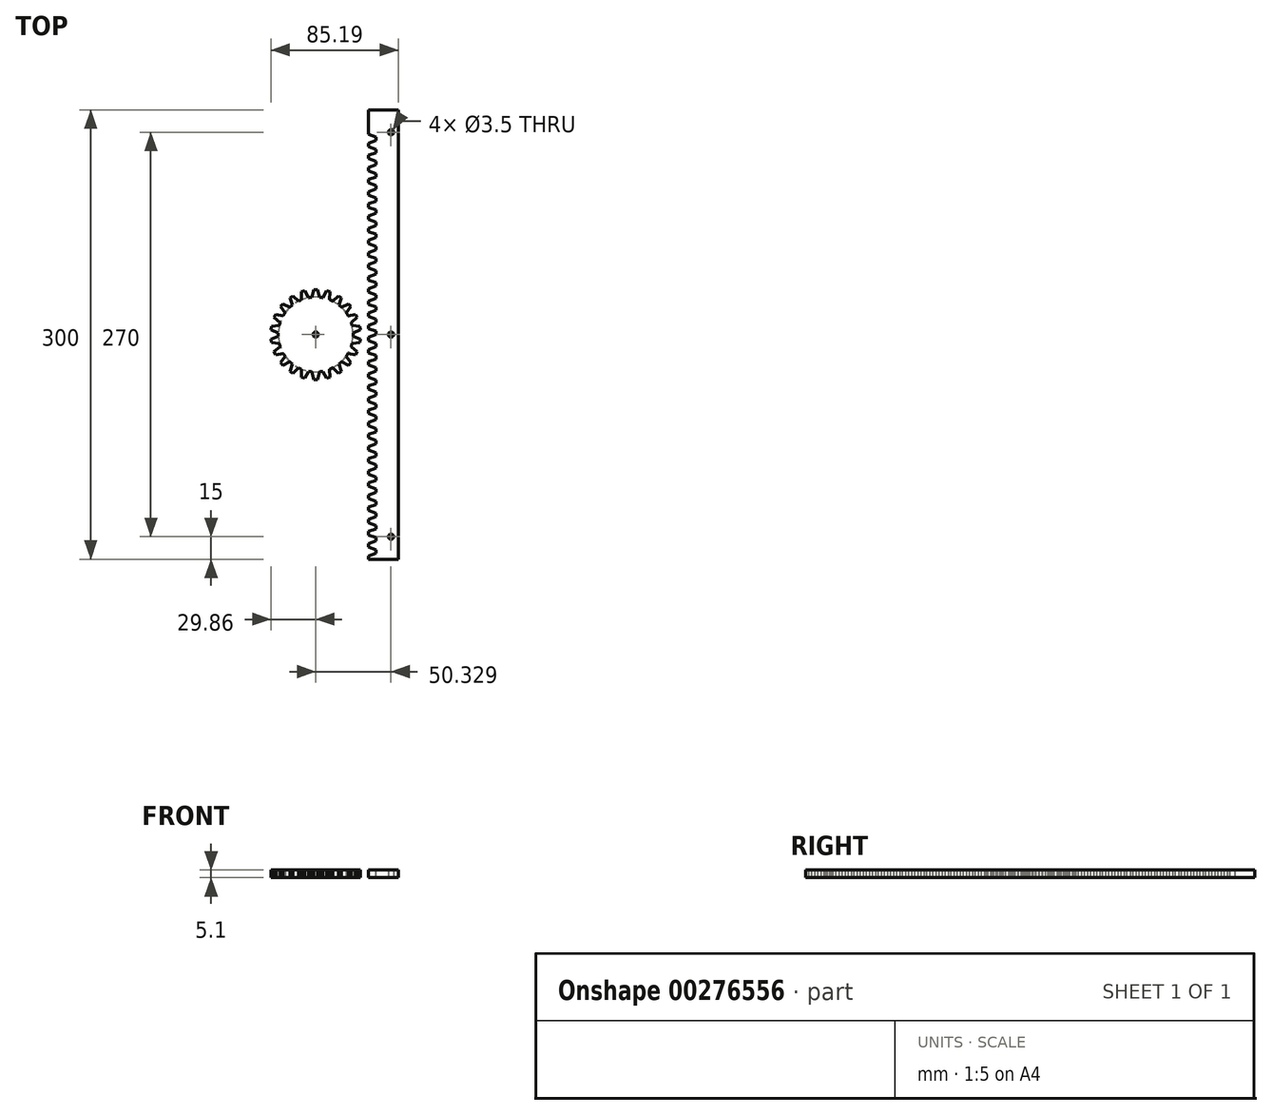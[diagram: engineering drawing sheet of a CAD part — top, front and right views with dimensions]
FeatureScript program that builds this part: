
annotation { "Feature Type Name" : "Feature", "Feature Type Description" : "" }
export const myFeature = defineFeature(function(context is Context, id is Id, definition is map)
    precondition{}
    {
        {
            var Q0;
            Q0=qCreatedBy(makeId("Top.planeOp"),FACE);
            var sketch = newSketch(context, id + "F0", { "sketchPlane" : qUnion([Q0])});
            skCircle(sketch, "E0", {"center": v(0, 0) * mm, "radius": 25 * mm});
            skSolve(sketch);
        }
        {
            var Q0;
            Q0 = qSketchRegion(id + "F0", true);
            extrude(context, id + "F1", {"entities" : qUnion([Q0]), "depth" : .1 * mm});
        }
        {
            var Q0;
            Q0=makeQuery(id+"F1.opExtrude","CAP_FACE",FACE,{"disambiguationData":[OSD([sQuery(id+"F0.wireOp",EDGE,"E0")])],"isStart":false});
            var sketch = newSketch(context, id + "F2", { "sketchPlane" : qUnion([Q0])});
            skLineSegment(sketch, "E1", {"start": v(0, 0) * mm, "end": v(3.22, 32.66) * mm, "construction": true});
            skLineSegment(sketch, "E2", {"start": v(0, 0) * mm, "end": v(-3.22, 32.7) * mm, "construction": true});
            skLineSegment(sketch, "E3", {"start": v(-2.45, 24.88) * mm, "end": v(-1.14, 30) * mm});
            skLineSegment(sketch, "E4", {"start": v(-1.14, 30) * mm, "end": v(1.14, 30) * mm});
            skLineSegment(sketch, "E5", {"start": v(1.14, 30) * mm, "end": v(2.45, 24.88) * mm});
            skLineSegment(sketch, "E6.1.0", {"start": v(-9.36, 23.18) * mm, "end": v(-9.54, 28.46) * mm});
            skLineSegment(sketch, "E6.1.1", {"start": v(-7.36, 29.1) * mm, "end": v(-4.66, 24.56) * mm});
            skLineSegment(sketch, "E6.1.2", {"start": v(-9.54, 28.46) * mm, "end": v(-7.36, 29.1) * mm});
            skLineSegment(sketch, "E6.2.0", {"start": v(-15.51, 19.6) * mm, "end": v(-17.18, 24.62) * mm});
            skLineSegment(sketch, "E6.2.1", {"start": v(-15.26, 25.85) * mm, "end": v(-11.39, 22.25) * mm});
            skLineSegment(sketch, "E6.2.2", {"start": v(-17.18, 24.62) * mm, "end": v(-15.26, 25.85) * mm});
            skLineSegment(sketch, "E6.3.0", {"start": v(-20.4, 14.44) * mm, "end": v(-23.42, 18.79) * mm});
            skLineSegment(sketch, "E6.3.1", {"start": v(-21.93, 20.5) * mm, "end": v(-17.2, 18.14) * mm});
            skLineSegment(sketch, "E6.3.2", {"start": v(-23.42, 18.79) * mm, "end": v(-21.93, 20.5) * mm});
            skLineSegment(sketch, "E6.4.0", {"start": v(-23.65, 8.1) * mm, "end": v(-27.76, 11.43) * mm});
            skLineSegment(sketch, "E6.4.1", {"start": v(-26.82, 13.5) * mm, "end": v(-21.61, 12.56) * mm});
            skLineSegment(sketch, "E6.4.2", {"start": v(-27.76, 11.43) * mm, "end": v(-26.82, 13.5) * mm});
            skLineSegment(sketch, "E6.5.0", {"start": v(-24.98, 1.12) * mm, "end": v(-29.86, 3.14) * mm});
            skLineSegment(sketch, "E6.5.1", {"start": v(-29.53, 5.4) * mm, "end": v(-24.28, 5.97) * mm});
            skLineSegment(sketch, "E6.5.2", {"start": v(-29.86, 3.14) * mm, "end": v(-29.53, 5.4) * mm});
            skLineSegment(sketch, "E6.6.0", {"start": v(-24.28, -5.97) * mm, "end": v(-29.53, -5.4) * mm});
            skLineSegment(sketch, "E6.6.1", {"start": v(-29.86, -3.14) * mm, "end": v(-24.98, -1.12) * mm});
            skLineSegment(sketch, "E6.6.2", {"start": v(-29.53, -5.4) * mm, "end": v(-29.86, -3.14) * mm});
            skLineSegment(sketch, "E6.7.0", {"start": v(-21.61, -12.56) * mm, "end": v(-26.82, -13.5) * mm});
            skLineSegment(sketch, "E6.7.1", {"start": v(-27.76, -11.43) * mm, "end": v(-23.65, -8.1) * mm});
            skLineSegment(sketch, "E6.7.2", {"start": v(-26.82, -13.5) * mm, "end": v(-27.76, -11.43) * mm});
            skLineSegment(sketch, "E6.8.0", {"start": v(-17.2, -18.14) * mm, "end": v(-21.93, -20.5) * mm});
            skLineSegment(sketch, "E6.8.1", {"start": v(-23.42, -18.79) * mm, "end": v(-20.4, -14.44) * mm});
            skLineSegment(sketch, "E6.8.2", {"start": v(-21.93, -20.5) * mm, "end": v(-23.42, -18.79) * mm});
            skLineSegment(sketch, "E6.9.0", {"start": v(-11.39, -22.25) * mm, "end": v(-15.26, -25.85) * mm});
            skLineSegment(sketch, "E6.9.1", {"start": v(-17.18, -24.62) * mm, "end": v(-15.51, -19.6) * mm});
            skLineSegment(sketch, "E6.9.2", {"start": v(-15.26, -25.85) * mm, "end": v(-17.18, -24.62) * mm});
            skLineSegment(sketch, "E6.10.0", {"start": v(-4.66, -24.56) * mm, "end": v(-7.36, -29.1) * mm});
            skLineSegment(sketch, "E6.10.1", {"start": v(-9.54, -28.46) * mm, "end": v(-9.36, -23.18) * mm});
            skLineSegment(sketch, "E6.10.2", {"start": v(-7.36, -29.1) * mm, "end": v(-9.54, -28.46) * mm});
            skLineSegment(sketch, "E6.11.0", {"start": v(2.45, -24.88) * mm, "end": v(1.14, -30) * mm});
            skLineSegment(sketch, "E6.11.1", {"start": v(-1.14, -30) * mm, "end": v(-2.45, -24.88) * mm});
            skLineSegment(sketch, "E6.11.2", {"start": v(1.14, -30) * mm, "end": v(-1.14, -30) * mm});
            skLineSegment(sketch, "E6.12.0", {"start": v(9.36, -23.18) * mm, "end": v(9.54, -28.46) * mm});
            skLineSegment(sketch, "E6.12.1", {"start": v(7.36, -29.1) * mm, "end": v(4.66, -24.56) * mm});
            skLineSegment(sketch, "E6.12.2", {"start": v(9.54, -28.46) * mm, "end": v(7.36, -29.1) * mm});
            skLineSegment(sketch, "E6.13.0", {"start": v(15.51, -19.6) * mm, "end": v(17.18, -24.62) * mm});
            skLineSegment(sketch, "E6.13.1", {"start": v(15.26, -25.85) * mm, "end": v(11.39, -22.25) * mm});
            skLineSegment(sketch, "E6.13.2", {"start": v(17.18, -24.62) * mm, "end": v(15.26, -25.85) * mm});
            skLineSegment(sketch, "E6.14.0", {"start": v(20.4, -14.44) * mm, "end": v(23.42, -18.79) * mm});
            skLineSegment(sketch, "E6.14.1", {"start": v(21.93, -20.5) * mm, "end": v(17.2, -18.14) * mm});
            skLineSegment(sketch, "E6.14.2", {"start": v(23.42, -18.79) * mm, "end": v(21.93, -20.5) * mm});
            skLineSegment(sketch, "E6.15.0", {"start": v(23.65, -8.1) * mm, "end": v(27.76, -11.43) * mm});
            skLineSegment(sketch, "E6.15.1", {"start": v(26.82, -13.5) * mm, "end": v(21.61, -12.56) * mm});
            skLineSegment(sketch, "E6.15.2", {"start": v(27.76, -11.43) * mm, "end": v(26.82, -13.5) * mm});
            skLineSegment(sketch, "E6.16.0", {"start": v(24.98, -1.12) * mm, "end": v(29.86, -3.14) * mm});
            skLineSegment(sketch, "E6.16.1", {"start": v(29.53, -5.4) * mm, "end": v(24.28, -5.97) * mm});
            skLineSegment(sketch, "E6.16.2", {"start": v(29.86, -3.14) * mm, "end": v(29.53, -5.4) * mm});
            skLineSegment(sketch, "E6.17.0", {"start": v(24.28, 5.97) * mm, "end": v(29.53, 5.4) * mm});
            skLineSegment(sketch, "E6.17.1", {"start": v(29.86, 3.14) * mm, "end": v(24.98, 1.12) * mm});
            skLineSegment(sketch, "E6.17.2", {"start": v(29.53, 5.4) * mm, "end": v(29.86, 3.14) * mm});
            skLineSegment(sketch, "E6.18.0", {"start": v(21.61, 12.56) * mm, "end": v(26.82, 13.5) * mm});
            skLineSegment(sketch, "E6.18.1", {"start": v(27.76, 11.43) * mm, "end": v(23.65, 8.1) * mm});
            skLineSegment(sketch, "E6.18.2", {"start": v(26.82, 13.5) * mm, "end": v(27.76, 11.43) * mm});
            skLineSegment(sketch, "E6.19.0", {"start": v(17.2, 18.14) * mm, "end": v(21.93, 20.5) * mm});
            skLineSegment(sketch, "E6.19.1", {"start": v(23.42, 18.79) * mm, "end": v(20.4, 14.44) * mm});
            skLineSegment(sketch, "E6.19.2", {"start": v(21.93, 20.5) * mm, "end": v(23.42, 18.79) * mm});
            skPoint(sketch, "E6.center", {"position": v(0, 0) * mm});
            skLineSegment(sketch, "E7.1.20.0", {"start": v(11.39, 22.25) * mm, "end": v(15.26, 25.85) * mm});
            skLineSegment(sketch, "E7.3.20.0", {"start": v(17.18, 24.62) * mm, "end": v(15.51, 19.6) * mm});
            skLineSegment(sketch, "E7.6.20.0", {"start": v(15.26, 25.85) * mm, "end": v(17.18, 24.62) * mm});
            skCircle(sketch, "E8", {"center": v(0, 0) * mm, "radius": 25.04 * mm});
            skLineSegment(sketch, "E9.1.21.0", {"start": v(4.66, 24.56) * mm, "end": v(7.36, 29.1) * mm});
            skLineSegment(sketch, "E9.3.21.0", {"start": v(9.54, 28.46) * mm, "end": v(9.36, 23.18) * mm});
            skLineSegment(sketch, "E9.6.21.0", {"start": v(7.36, 29.1) * mm, "end": v(9.54, 28.46) * mm});
            skSolve(sketch);
        }
        {
            var Q0;
            Q0 = qSketchRegion(id + "F2", true);
            extrude(context, id + "F3", {"entities" : qUnion([Q0]), "operationType" : NewBodyOperationType.ADD, "depth" : 5 * mm});
        }
        {
            var Q0;
            Q0=qCreatedBy(makeId("Top.planeOp"),FACE);
            var sketch = newSketch(context, id + "F4", { "sketchPlane" : qUnion([Q0])});
            skLineSegment(sketch, "E10.bottom", {"start": v(35.33, -150) * mm, "end": v(55.33, -150) * mm});
            skLineSegment(sketch, "E10.top", {"start": v(35.33, 150) * mm, "end": v(55.33, 150) * mm});
            skLineSegment(sketch, "E10.left", {"start": v(35.33, -150) * mm, "end": v(35.33, 150) * mm});
            skLineSegment(sketch, "E10.right", {"start": v(55.33, -150) * mm, "end": v(55.33, 150) * mm});
            skPoint(sketch, "E10.middle", {"position": v(45.33, 0) * mm});
            skSolve(sketch);
        }
        {
            var Q0;
            Q0 = qSketchRegion(id + "F4", true);
            extrude(context, id + "F5", {"entities" : qUnion([Q0]), "depth" : 5 * mm});
        }
        {
            var Q0;
            Q0=makeQuery(id+"F5.opExtrude","CAP_FACE",FACE,{"disambiguationData":[OSD([sQuery(id+"F4.wireOp",EDGE,"E10.bottom"),sQuery(id+"F4.wireOp",EDGE,"E10.top"),sQuery(id+"F4.wireOp",EDGE,"E10.left"),sQuery(id+"F4.wireOp",EDGE,"E10.right")])],"isStart":false});
            var sketch = newSketch(context, id + "F6", { "sketchPlane" : qUnion([Q0])});
            skLineSegment(sketch, "E11", {"start": v(35.33, -147.77) * mm, "end": v(40.33, -145.95) * mm});
            skLineSegment(sketch, "E12", {"start": v(40.33, -145.95) * mm, "end": v(40.33, -143.72) * mm});
            skLineSegment(sketch, "E13", {"start": v(40.33, -143.72) * mm, "end": v(35.33, -141.9) * mm});
            skLineSegment(sketch, "E14", {"start": v(35.33, -147.77) * mm, "end": v(35.33, -150) * mm});
            skLineSegment(sketch, "E15.1.0.0", {"start": v(40.33, -135.62) * mm, "end": v(35.33, -133.8) * mm});
            skLineSegment(sketch, "E15.1.0.1", {"start": v(35.33, -139.67) * mm, "end": v(40.33, -137.85) * mm});
            skLineSegment(sketch, "E15.1.0.2", {"start": v(35.33, -139.67) * mm, "end": v(35.33, -141.9) * mm});
            skLineSegment(sketch, "E15.1.0.3", {"start": v(40.33, -137.85) * mm, "end": v(40.33, -135.62) * mm});
            skLineSegment(sketch, "E15.2.0.0", {"start": v(40.33, -127.51) * mm, "end": v(35.33, -125.7) * mm});
            skLineSegment(sketch, "E15.2.0.1", {"start": v(35.33, -131.56) * mm, "end": v(40.33, -129.75) * mm});
            skLineSegment(sketch, "E15.2.0.2", {"start": v(35.33, -131.56) * mm, "end": v(35.33, -133.8) * mm});
            skLineSegment(sketch, "E15.2.0.3", {"start": v(40.33, -129.75) * mm, "end": v(40.33, -127.51) * mm});
            skLineSegment(sketch, "E15.3.0.0", {"start": v(40.33, -119.41) * mm, "end": v(35.33, -117.6) * mm});
            skLineSegment(sketch, "E15.3.0.1", {"start": v(35.33, -123.46) * mm, "end": v(40.33, -121.64) * mm});
            skLineSegment(sketch, "E15.3.0.2", {"start": v(35.33, -123.46) * mm, "end": v(35.33, -125.7) * mm});
            skLineSegment(sketch, "E15.3.0.3", {"start": v(40.33, -121.64) * mm, "end": v(40.33, -119.41) * mm});
            skLineSegment(sketch, "E15.4.0.0", {"start": v(40.33, -111.31) * mm, "end": v(35.33, -109.5) * mm});
            skLineSegment(sketch, "E15.4.0.1", {"start": v(35.33, -115.36) * mm, "end": v(40.33, -113.54) * mm});
            skLineSegment(sketch, "E15.4.0.2", {"start": v(35.33, -115.36) * mm, "end": v(35.33, -117.6) * mm});
            skLineSegment(sketch, "E15.4.0.3", {"start": v(40.33, -113.54) * mm, "end": v(40.33, -111.31) * mm});
            skLineSegment(sketch, "E15.5.0.0", {"start": v(40.33, -103.2) * mm, "end": v(35.33, -101.39) * mm});
            skLineSegment(sketch, "E15.5.0.1", {"start": v(35.33, -107.26) * mm, "end": v(40.33, -105.44) * mm});
            skLineSegment(sketch, "E15.5.0.2", {"start": v(35.33, -107.26) * mm, "end": v(35.33, -109.5) * mm});
            skLineSegment(sketch, "E15.5.0.3", {"start": v(40.33, -105.44) * mm, "end": v(40.33, -103.2) * mm});
            skLineSegment(sketch, "E15.6.0.0", {"start": v(40.33, -95.1) * mm, "end": v(35.33, -93.29) * mm});
            skLineSegment(sketch, "E15.6.0.1", {"start": v(35.33, -99.16) * mm, "end": v(40.33, -97.34) * mm});
            skLineSegment(sketch, "E15.6.0.2", {"start": v(35.33, -99.16) * mm, "end": v(35.33, -101.39) * mm});
            skLineSegment(sketch, "E15.6.0.3", {"start": v(40.33, -97.34) * mm, "end": v(40.33, -95.1) * mm});
            skLineSegment(sketch, "E15.7.0.0", {"start": v(40.33, -87) * mm, "end": v(35.33, -85.18) * mm});
            skLineSegment(sketch, "E15.7.0.1", {"start": v(35.33, -91.05) * mm, "end": v(40.33, -89.24) * mm});
            skLineSegment(sketch, "E15.7.0.2", {"start": v(35.33, -91.05) * mm, "end": v(35.33, -93.29) * mm});
            skLineSegment(sketch, "E15.7.0.3", {"start": v(40.33, -89.24) * mm, "end": v(40.33, -87) * mm});
            skLineSegment(sketch, "E15.8.0.0", {"start": v(40.33, -78.9) * mm, "end": v(35.33, -77.08) * mm});
            skLineSegment(sketch, "E15.8.0.1", {"start": v(35.33, -82.95) * mm, "end": v(40.33, -81.13) * mm});
            skLineSegment(sketch, "E15.8.0.2", {"start": v(35.33, -82.95) * mm, "end": v(35.33, -85.18) * mm});
            skLineSegment(sketch, "E15.8.0.3", {"start": v(40.33, -81.13) * mm, "end": v(40.33, -78.9) * mm});
            skLineSegment(sketch, "E15.9.0.0", {"start": v(40.33, -70.8) * mm, "end": v(35.33, -68.98) * mm});
            skLineSegment(sketch, "E15.9.0.1", {"start": v(35.33, -74.85) * mm, "end": v(40.33, -73.03) * mm});
            skLineSegment(sketch, "E15.9.0.2", {"start": v(35.33, -74.85) * mm, "end": v(35.33, -77.08) * mm});
            skLineSegment(sketch, "E15.9.0.3", {"start": v(40.33, -73.03) * mm, "end": v(40.33, -70.8) * mm});
            skLineSegment(sketch, "E15.10.0.0", {"start": v(40.33, -62.7) * mm, "end": v(35.33, -60.88) * mm});
            skLineSegment(sketch, "E15.10.0.1", {"start": v(35.33, -66.75) * mm, "end": v(40.33, -64.93) * mm});
            skLineSegment(sketch, "E15.10.0.2", {"start": v(35.33, -66.75) * mm, "end": v(35.33, -68.98) * mm});
            skLineSegment(sketch, "E15.10.0.3", {"start": v(40.33, -64.93) * mm, "end": v(40.33, -62.7) * mm});
            skLineSegment(sketch, "E15.11.0.0", {"start": v(40.33, -54.6) * mm, "end": v(35.33, -52.78) * mm});
            skLineSegment(sketch, "E15.11.0.1", {"start": v(35.33, -58.65) * mm, "end": v(40.33, -56.83) * mm});
            skLineSegment(sketch, "E15.11.0.2", {"start": v(35.33, -58.65) * mm, "end": v(35.33, -60.88) * mm});
            skLineSegment(sketch, "E15.11.0.3", {"start": v(40.33, -56.83) * mm, "end": v(40.33, -54.6) * mm});
            skLineSegment(sketch, "E15.12.0.0", {"start": v(40.33, -46.5) * mm, "end": v(35.33, -44.67) * mm});
            skLineSegment(sketch, "E15.12.0.1", {"start": v(35.33, -50.54) * mm, "end": v(40.33, -48.73) * mm});
            skLineSegment(sketch, "E15.12.0.2", {"start": v(35.33, -50.54) * mm, "end": v(35.33, -52.78) * mm});
            skLineSegment(sketch, "E15.12.0.3", {"start": v(40.33, -48.73) * mm, "end": v(40.33, -46.5) * mm});
            skLineSegment(sketch, "E15.13.0.0", {"start": v(40.33, -38.4) * mm, "end": v(35.33, -36.57) * mm});
            skLineSegment(sketch, "E15.13.0.1", {"start": v(35.33, -42.44) * mm, "end": v(40.33, -40.62) * mm});
            skLineSegment(sketch, "E15.13.0.2", {"start": v(35.33, -42.44) * mm, "end": v(35.33, -44.67) * mm});
            skLineSegment(sketch, "E15.13.0.3", {"start": v(40.33, -40.62) * mm, "end": v(40.33, -38.4) * mm});
            skLineSegment(sketch, "E15.14.0.0", {"start": v(40.33, -30.3) * mm, "end": v(35.33, -28.47) * mm});
            skLineSegment(sketch, "E15.14.0.1", {"start": v(35.33, -34.34) * mm, "end": v(40.33, -32.52) * mm});
            skLineSegment(sketch, "E15.14.0.2", {"start": v(35.33, -34.34) * mm, "end": v(35.33, -36.57) * mm});
            skLineSegment(sketch, "E15.14.0.3", {"start": v(40.33, -32.52) * mm, "end": v(40.33, -30.3) * mm});
            skLineSegment(sketch, "E15.15.0.0", {"start": v(40.33, -22.19) * mm, "end": v(35.33, -20.37) * mm});
            skLineSegment(sketch, "E15.15.0.1", {"start": v(35.33, -26.24) * mm, "end": v(40.33, -24.42) * mm});
            skLineSegment(sketch, "E15.15.0.2", {"start": v(35.33, -26.24) * mm, "end": v(35.33, -28.47) * mm});
            skLineSegment(sketch, "E15.15.0.3", {"start": v(40.33, -24.42) * mm, "end": v(40.33, -22.19) * mm});
            skLineSegment(sketch, "E15.16.0.0", {"start": v(40.33, -14.09) * mm, "end": v(35.33, -12.27) * mm});
            skLineSegment(sketch, "E15.16.0.1", {"start": v(35.33, -18.14) * mm, "end": v(40.33, -16.32) * mm});
            skLineSegment(sketch, "E15.16.0.2", {"start": v(35.33, -18.14) * mm, "end": v(35.33, -20.37) * mm});
            skLineSegment(sketch, "E15.16.0.3", {"start": v(40.33, -16.32) * mm, "end": v(40.33, -14.09) * mm});
            skLineSegment(sketch, "E15.17.0.0", {"start": v(40.33, -5.98) * mm, "end": v(35.33, -4.16) * mm});
            skLineSegment(sketch, "E15.17.0.1", {"start": v(35.33, -10.03) * mm, "end": v(40.33, -8.22) * mm});
            skLineSegment(sketch, "E15.17.0.2", {"start": v(35.33, -10.03) * mm, "end": v(35.33, -12.27) * mm});
            skLineSegment(sketch, "E15.17.0.3", {"start": v(40.33, -8.22) * mm, "end": v(40.33, -5.98) * mm});
            skLineSegment(sketch, "E15.18.0.0", {"start": v(40.33, 2.12) * mm, "end": v(35.33, 3.94) * mm});
            skLineSegment(sketch, "E15.18.0.1", {"start": v(35.33, -1.93) * mm, "end": v(40.33, -0.11) * mm});
            skLineSegment(sketch, "E15.18.0.2", {"start": v(35.33, -1.93) * mm, "end": v(35.33, -4.16) * mm});
            skLineSegment(sketch, "E15.18.0.3", {"start": v(40.33, -0.11) * mm, "end": v(40.33, 2.12) * mm});
            skLineSegment(sketch, "E15.19.0.0", {"start": v(40.33, 10.22) * mm, "end": v(35.33, 12.04) * mm});
            skLineSegment(sketch, "E15.19.0.1", {"start": v(35.33, 6.17) * mm, "end": v(40.33, 7.99) * mm});
            skLineSegment(sketch, "E15.19.0.2", {"start": v(35.33, 6.17) * mm, "end": v(35.33, 3.94) * mm});
            skLineSegment(sketch, "E15.19.0.3", {"start": v(40.33, 7.99) * mm, "end": v(40.33, 10.22) * mm});
            skLineSegment(sketch, "E15.20.0.0", {"start": v(40.33, 18.32) * mm, "end": v(35.33, 20.14) * mm});
            skLineSegment(sketch, "E15.20.0.1", {"start": v(35.33, 14.27) * mm, "end": v(40.33, 16.1) * mm});
            skLineSegment(sketch, "E15.20.0.2", {"start": v(35.33, 14.27) * mm, "end": v(35.33, 12.04) * mm});
            skLineSegment(sketch, "E15.20.0.3", {"start": v(40.33, 16.1) * mm, "end": v(40.33, 18.32) * mm});
            skLineSegment(sketch, "E15.21.0.0", {"start": v(40.33, 26.42) * mm, "end": v(35.33, 28.24) * mm});
            skLineSegment(sketch, "E15.21.0.1", {"start": v(35.33, 22.37) * mm, "end": v(40.33, 24.2) * mm});
            skLineSegment(sketch, "E15.21.0.2", {"start": v(35.33, 22.37) * mm, "end": v(35.33, 20.14) * mm});
            skLineSegment(sketch, "E15.21.0.3", {"start": v(40.33, 24.2) * mm, "end": v(40.33, 26.42) * mm});
            skLineSegment(sketch, "E15.22.0.0", {"start": v(40.33, 34.53) * mm, "end": v(35.33, 36.35) * mm});
            skLineSegment(sketch, "E15.22.0.1", {"start": v(35.33, 30.48) * mm, "end": v(40.33, 32.3) * mm});
            skLineSegment(sketch, "E15.22.0.2", {"start": v(35.33, 30.48) * mm, "end": v(35.33, 28.24) * mm});
            skLineSegment(sketch, "E15.22.0.3", {"start": v(40.33, 32.3) * mm, "end": v(40.33, 34.53) * mm});
            skLineSegment(sketch, "E15.23.0.0", {"start": v(40.33, 42.63) * mm, "end": v(35.33, 44.45) * mm});
            skLineSegment(sketch, "E15.23.0.1", {"start": v(35.33, 38.58) * mm, "end": v(40.33, 40.4) * mm});
            skLineSegment(sketch, "E15.23.0.2", {"start": v(35.33, 38.58) * mm, "end": v(35.33, 36.35) * mm});
            skLineSegment(sketch, "E15.23.0.3", {"start": v(40.33, 40.4) * mm, "end": v(40.33, 42.63) * mm});
            skLineSegment(sketch, "E15.24.0.0", {"start": v(40.33, 50.73) * mm, "end": v(35.33, 52.55) * mm});
            skLineSegment(sketch, "E15.24.0.1", {"start": v(35.33, 46.68) * mm, "end": v(40.33, 48.5) * mm});
            skLineSegment(sketch, "E15.24.0.2", {"start": v(35.33, 46.68) * mm, "end": v(35.33, 44.45) * mm});
            skLineSegment(sketch, "E15.24.0.3", {"start": v(40.33, 48.5) * mm, "end": v(40.33, 50.73) * mm});
            skLineSegment(sketch, "E15.25.0.0", {"start": v(40.33, 58.83) * mm, "end": v(35.33, 60.65) * mm});
            skLineSegment(sketch, "E15.25.0.1", {"start": v(35.33, 54.78) * mm, "end": v(40.33, 56.6) * mm});
            skLineSegment(sketch, "E15.25.0.2", {"start": v(35.33, 54.78) * mm, "end": v(35.33, 52.55) * mm});
            skLineSegment(sketch, "E15.25.0.3", {"start": v(40.33, 56.6) * mm, "end": v(40.33, 58.83) * mm});
            skLineSegment(sketch, "E15.26.0.0", {"start": v(40.33, 66.93) * mm, "end": v(35.33, 68.75) * mm});
            skLineSegment(sketch, "E15.26.0.1", {"start": v(35.33, 62.88) * mm, "end": v(40.33, 64.7) * mm});
            skLineSegment(sketch, "E15.26.0.2", {"start": v(35.33, 62.88) * mm, "end": v(35.33, 60.65) * mm});
            skLineSegment(sketch, "E15.26.0.3", {"start": v(40.33, 64.7) * mm, "end": v(40.33, 66.93) * mm});
            skLineSegment(sketch, "E15.27.0.0", {"start": v(40.33, 75.04) * mm, "end": v(35.33, 76.86) * mm});
            skLineSegment(sketch, "E15.27.0.1", {"start": v(35.33, 70.99) * mm, "end": v(40.33, 72.8) * mm});
            skLineSegment(sketch, "E15.27.0.2", {"start": v(35.33, 70.99) * mm, "end": v(35.33, 68.75) * mm});
            skLineSegment(sketch, "E15.27.0.3", {"start": v(40.33, 72.8) * mm, "end": v(40.33, 75.04) * mm});
            skLineSegment(sketch, "E15.28.0.0", {"start": v(40.33, 83.14) * mm, "end": v(35.33, 84.96) * mm});
            skLineSegment(sketch, "E15.28.0.1", {"start": v(35.33, 79.09) * mm, "end": v(40.33, 80.9) * mm});
            skLineSegment(sketch, "E15.28.0.2", {"start": v(35.33, 79.09) * mm, "end": v(35.33, 76.86) * mm});
            skLineSegment(sketch, "E15.28.0.3", {"start": v(40.33, 80.9) * mm, "end": v(40.33, 83.14) * mm});
            skLineSegment(sketch, "E15.29.0.0", {"start": v(40.33, 91.24) * mm, "end": v(35.33, 93.06) * mm});
            skLineSegment(sketch, "E15.29.0.1", {"start": v(35.33, 87.19) * mm, "end": v(40.33, 89) * mm});
            skLineSegment(sketch, "E15.29.0.2", {"start": v(35.33, 87.19) * mm, "end": v(35.33, 84.96) * mm});
            skLineSegment(sketch, "E15.29.0.3", {"start": v(40.33, 89) * mm, "end": v(40.33, 91.24) * mm});
            skLineSegment(sketch, "E15.direction1", {"start": v(35.33, -141.9) * mm, "end": v(35.33, -133.8) * mm, "construction": true});
            skLineSegment(sketch, "E16.0.30.0", {"start": v(40.33, 99.34) * mm, "end": v(35.33, 101.16) * mm});
            skLineSegment(sketch, "E16.3.30.0", {"start": v(35.33, 95.3) * mm, "end": v(40.33, 97.11) * mm});
            skLineSegment(sketch, "E16.6.30.0", {"start": v(35.33, 95.3) * mm, "end": v(35.33, 93.06) * mm});
            skLineSegment(sketch, "E16.9.30.0", {"start": v(40.33, 97.11) * mm, "end": v(40.33, 99.34) * mm});
            skLineSegment(sketch, "E16.0.31.0", {"start": v(40.33, 107.44) * mm, "end": v(35.33, 109.26) * mm});
            skLineSegment(sketch, "E16.3.31.0", {"start": v(35.33, 103.4) * mm, "end": v(40.33, 105.21) * mm});
            skLineSegment(sketch, "E16.6.31.0", {"start": v(35.33, 103.4) * mm, "end": v(35.33, 101.16) * mm});
            skLineSegment(sketch, "E16.9.31.0", {"start": v(40.33, 105.21) * mm, "end": v(40.33, 107.44) * mm});
            skLineSegment(sketch, "E16.0.32.0", {"start": v(40.33, 115.55) * mm, "end": v(35.33, 117.37) * mm});
            skLineSegment(sketch, "E16.3.32.0", {"start": v(35.33, 111.5) * mm, "end": v(40.33, 113.31) * mm});
            skLineSegment(sketch, "E16.6.32.0", {"start": v(35.33, 111.5) * mm, "end": v(35.33, 109.26) * mm});
            skLineSegment(sketch, "E16.9.32.0", {"start": v(40.33, 113.31) * mm, "end": v(40.33, 115.55) * mm});
            skLineSegment(sketch, "E16.0.33.0", {"start": v(40.33, 123.65) * mm, "end": v(35.33, 125.47) * mm});
            skLineSegment(sketch, "E16.3.33.0", {"start": v(35.33, 119.6) * mm, "end": v(40.33, 121.42) * mm});
            skLineSegment(sketch, "E16.6.33.0", {"start": v(35.33, 119.6) * mm, "end": v(35.33, 117.37) * mm});
            skLineSegment(sketch, "E16.9.33.0", {"start": v(40.33, 121.42) * mm, "end": v(40.33, 123.65) * mm});
            skLineSegment(sketch, "E16.0.34.0", {"start": v(40.33, 131.75) * mm, "end": v(35.33, 133.57) * mm});
            skLineSegment(sketch, "E16.3.34.0", {"start": v(35.33, 127.7) * mm, "end": v(40.33, 129.52) * mm});
            skLineSegment(sketch, "E16.6.34.0", {"start": v(35.33, 127.7) * mm, "end": v(35.33, 125.47) * mm});
            skLineSegment(sketch, "E16.9.34.0", {"start": v(40.33, 129.52) * mm, "end": v(40.33, 131.75) * mm});
            skLineSegment(sketch, "E17", {"start": v(35.33, -150) * mm, "end": v(35.33, 133.57) * mm});
            skSolve(sketch);
        }
        {
            var Q0;
            Q0 = qSketchRegion(id + "F6", true);
            extrude(context, id + "F7", {"entities" : qUnion([Q0]), "operationType" : NewBodyOperationType.REMOVE, "oppositeDirection" : true, "depth" : 5 * mm});
        }
        {
            var Q0;
            Q0=makeQuery(id+"F5.opExtrude","CAP_FACE",FACE,{"disambiguationData":[OSD([sQuery(id+"F4.wireOp",EDGE,"E10.bottom"),sQuery(id+"F4.wireOp",EDGE,"E10.top"),sQuery(id+"F4.wireOp",EDGE,"E10.left"),sQuery(id+"F4.wireOp",EDGE,"E10.right")])],"isStart":false});
            var sketch = newSketch(context, id + "F8", { "sketchPlane" : qUnion([Q0])});
            skPoint(sketch, "E18", {"position": v(50.33, -135) * mm});
            skPoint(sketch, "E19", {"position": v(50.33, 0) * mm});
            skPoint(sketch, "E20", {"position": v(50.33, 135) * mm});
            skSolve(sketch);
        }
        {
            var Q0;
            Q0=makeQuery(id+"F3.opExtrude","CAP_FACE",FACE,{"disambiguationData":[OSD([sQuery(id+"F2.wireOp",EDGE,"E3"),sQuery(id+"F2.wireOp",EDGE,"E4"),sQuery(id+"F2.wireOp",EDGE,"E5"),sQuery(id+"F2.wireOp",EDGE,"E6.1.0"),sQuery(id+"F2.wireOp",EDGE,"E6.1.1"),sQuery(id+"F2.wireOp",EDGE,"E6.1.2"),sQuery(id+"F2.wireOp",EDGE,"E6.2.0"),sQuery(id+"F2.wireOp",EDGE,"E6.2.1"),sQuery(id+"F2.wireOp",EDGE,"E6.2.2"),sQuery(id+"F2.wireOp",EDGE,"E6.3.0"),sQuery(id+"F2.wireOp",EDGE,"E6.3.1"),sQuery(id+"F2.wireOp",EDGE,"E6.3.2"),sQuery(id+"F2.wireOp",EDGE,"E6.4.0"),sQuery(id+"F2.wireOp",EDGE,"E6.4.1"),sQuery(id+"F2.wireOp",EDGE,"E6.4.2"),sQuery(id+"F2.wireOp",EDGE,"E6.5.0"),sQuery(id+"F2.wireOp",EDGE,"E6.5.1"),sQuery(id+"F2.wireOp",EDGE,"E6.5.2"),sQuery(id+"F2.wireOp",EDGE,"E6.6.0"),sQuery(id+"F2.wireOp",EDGE,"E6.6.1"),sQuery(id+"F2.wireOp",EDGE,"E6.6.2"),sQuery(id+"F2.wireOp",EDGE,"E6.7.0"),sQuery(id+"F2.wireOp",EDGE,"E6.7.1"),sQuery(id+"F2.wireOp",EDGE,"E6.7.2"),sQuery(id+"F2.wireOp",EDGE,"E6.8.0"),sQuery(id+"F2.wireOp",EDGE,"E6.8.1"),sQuery(id+"F2.wireOp",EDGE,"E6.8.2"),sQuery(id+"F2.wireOp",EDGE,"E6.9.0"),sQuery(id+"F2.wireOp",EDGE,"E6.9.1"),sQuery(id+"F2.wireOp",EDGE,"E6.9.2"),sQuery(id+"F2.wireOp",EDGE,"E6.10.0"),sQuery(id+"F2.wireOp",EDGE,"E6.10.1"),sQuery(id+"F2.wireOp",EDGE,"E6.10.2"),sQuery(id+"F2.wireOp",EDGE,"E6.11.0"),sQuery(id+"F2.wireOp",EDGE,"E6.11.1"),sQuery(id+"F2.wireOp",EDGE,"E6.11.2"),sQuery(id+"F2.wireOp",EDGE,"E6.12.0"),sQuery(id+"F2.wireOp",EDGE,"E6.12.1"),sQuery(id+"F2.wireOp",EDGE,"E6.12.2"),sQuery(id+"F2.wireOp",EDGE,"E6.13.0"),sQuery(id+"F2.wireOp",EDGE,"E6.13.1"),sQuery(id+"F2.wireOp",EDGE,"E6.13.2"),sQuery(id+"F2.wireOp",EDGE,"E6.14.0"),sQuery(id+"F2.wireOp",EDGE,"E6.14.1"),sQuery(id+"F2.wireOp",EDGE,"E6.14.2"),sQuery(id+"F2.wireOp",EDGE,"E6.15.0"),sQuery(id+"F2.wireOp",EDGE,"E6.15.1"),sQuery(id+"F2.wireOp",EDGE,"E6.15.2"),sQuery(id+"F2.wireOp",EDGE,"E6.16.0"),sQuery(id+"F2.wireOp",EDGE,"E6.16.1"),sQuery(id+"F2.wireOp",EDGE,"E6.16.2"),sQuery(id+"F2.wireOp",EDGE,"E6.17.0"),sQuery(id+"F2.wireOp",EDGE,"E6.17.1"),sQuery(id+"F2.wireOp",EDGE,"E6.17.2"),sQuery(id+"F2.wireOp",EDGE,"E6.18.0"),sQuery(id+"F2.wireOp",EDGE,"E6.18.1"),sQuery(id+"F2.wireOp",EDGE,"E6.18.2"),sQuery(id+"F2.wireOp",EDGE,"E6.19.0"),sQuery(id+"F2.wireOp",EDGE,"E6.19.1"),sQuery(id+"F2.wireOp",EDGE,"E6.19.2"),sQuery(id+"F2.wireOp",EDGE,"E7.1.20.0"),sQuery(id+"F2.wireOp",EDGE,"E7.3.20.0"),sQuery(id+"F2.wireOp",EDGE,"E7.6.20.0"),sQuery(id+"F2.wireOp",EDGE,"E8"),sQuery(id+"F2.wireOp",EDGE,"E9.1.21.0"),sQuery(id+"F2.wireOp",EDGE,"E9.3.21.0"),sQuery(id+"F2.wireOp",EDGE,"E9.6.21.0")])],"isStart":false});
            var sketch = newSketch(context, id + "F9", { "sketchPlane" : qUnion([Q0])});
            skPoint(sketch, "E21", {"position": v(0, 0) * mm});
            skSolve(sketch);
        }
        {
            var Q0;
            Q0=sQuery(id+"F9.wireOp",VERTEX,"E21");
            var Q1;
            Q1=makeQuery(id+"F1.opExtrude","SWEPT_BODY",BODY,{"disambiguationData":[OSD([sQuery(id+"F0.wireOp",EDGE,"E0")])]});
            var Q2;
            Q2=makeQuery(id+"F5.opExtrude","SWEPT_BODY",BODY,{"disambiguationData":[OSD([sQuery(id+"F4.wireOp",EDGE,"E10.bottom"),sQuery(id+"F4.wireOp",EDGE,"E10.top"),sQuery(id+"F4.wireOp",EDGE,"E10.left"),sQuery(id+"F4.wireOp",EDGE,"E10.right")])]});
            hole(context, id + "F10", {"style" : HoleStyle.SIMPLE, "endStyle" : HoleEndStyle.THROUGH, "holeDiameter" : 3.5 * mm, "tappedDepth" : 12 * mm, "tapClearance" : 3, "locations" : qUnion([Q0]), "scope" : qUnion([Q1, Q2])});
        }
        {
            var Q0;
            Q0=sQuery(id+"F8.wireOp",VERTEX,"E20");
            var Q1;
            Q1=sQuery(id+"F8.wireOp",VERTEX,"E19");
            var Q2;
            Q2=sQuery(id+"F8.wireOp",VERTEX,"E18");
            var Q3;
            Q3=makeQuery(id+"F5.opExtrude","SWEPT_BODY",BODY,{"disambiguationData":[OSD([sQuery(id+"F4.wireOp",EDGE,"E10.bottom"),sQuery(id+"F4.wireOp",EDGE,"E10.top"),sQuery(id+"F4.wireOp",EDGE,"E10.left"),sQuery(id+"F4.wireOp",EDGE,"E10.right")])]});
            hole(context, id + "F11", {"style" : HoleStyle.SIMPLE, "endStyle" : HoleEndStyle.THROUGH, "holeDiameter" : 3.5 * mm, "isTappedThrough" : true, "tappedDepth" : 12 * mm, "tapClearance" : 3, "locations" : qUnion([Q0, Q1, Q2]), "scope" : qUnion([Q3])});
        }
    });
